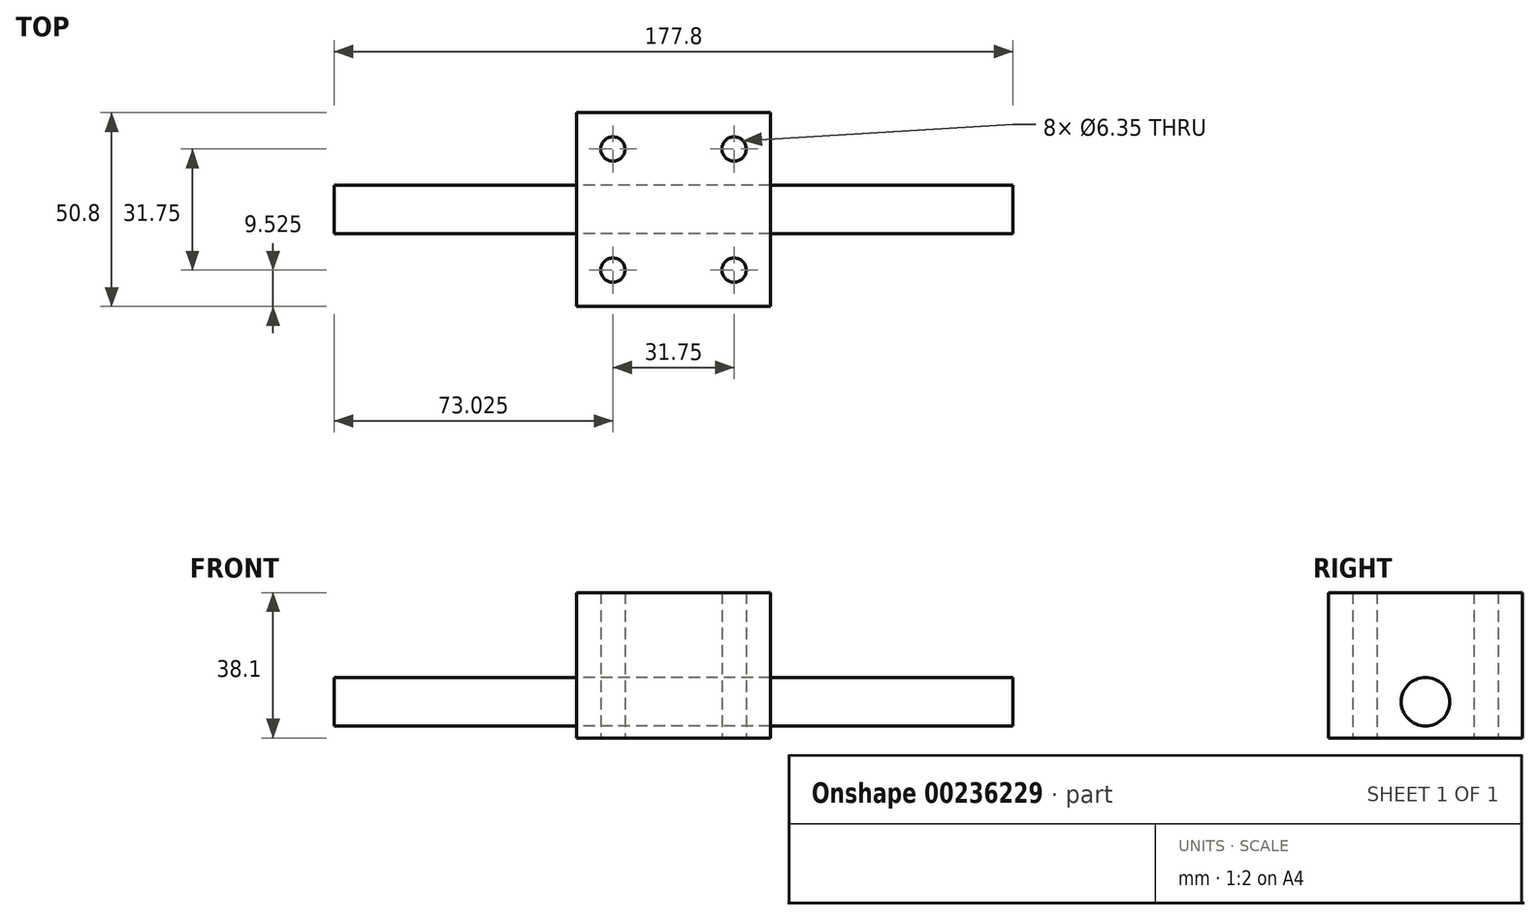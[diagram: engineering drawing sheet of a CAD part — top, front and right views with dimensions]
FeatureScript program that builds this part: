
annotation { "Feature Type Name" : "Feature", "Feature Type Description" : "" }
export const myFeature = defineFeature(function(context is Context, id is Id, definition is map)
    precondition{}
    {
        {
            var Q0;
            Q0=qCreatedBy(makeId("Top.planeOp"),FACE);
            var sketch = newSketch(context, id + "F0", { "sketchPlane" : qUnion([Q0])});
            skLineSegment(sketch, "E0.bottom", {"start": v(25.4, -25.4) * mm, "end": v(-25.4, -25.4) * mm});
            skLineSegment(sketch, "E0.top", {"start": v(25.4, 25.4) * mm, "end": v(-25.4, 25.4) * mm});
            skLineSegment(sketch, "E0.left", {"start": v(25.4, -25.4) * mm, "end": v(25.4, 25.4) * mm});
            skLineSegment(sketch, "E0.right", {"start": v(-25.4, -25.4) * mm, "end": v(-25.4, 25.4) * mm});
            skPoint(sketch, "E0.middle", {"position": v(0, 0) * mm});
            skCircle(sketch, "E1", {"center": v(-15.88, 15.87) * mm, "radius": 3.18 * mm});
            skCircle(sketch, "E2.MirrorC", {"center": v(15.88, 15.87) * mm, "radius": 3.18 * mm});
            skCircle(sketch, "E3.MirrorC", {"center": v(15.88, -15.87) * mm, "radius": 3.18 * mm});
            skCircle(sketch, "E4.MirrorC", {"center": v(-15.88, -15.87) * mm, "radius": 3.18 * mm});
            skSolve(sketch);
        }
        {
            var Q0;
            Q0 = qSketchRegion(id + "F0", true);
            extrude(context, id + "F1", {"entities" : qUnion([Q0]), "endBound" : BoundingType.SYMMETRIC, "depth" : 38.1 * mm});
        }
        {
            var Q0;
            Q0=makeQuery(id+"F1.opExtrude","SWEPT_BODY",BODY,{"disambiguationData":[OSD([sQuery(id+"F0.wireOp",EDGE,"E0.bottom"),sQuery(id+"F0.wireOp",EDGE,"E0.top"),sQuery(id+"F0.wireOp",EDGE,"E0.left"),sQuery(id+"F0.wireOp",EDGE,"E0.right"),sQuery(id+"F0.wireOp",EDGE,"E1"),sQuery(id+"F0.wireOp",EDGE,"E2.MirrorC"),sQuery(id+"F0.wireOp",EDGE,"E3.MirrorC"),sQuery(id+"F0.wireOp",EDGE,"E4.MirrorC")])]});
            var Q1;
            Q1=qCreatedBy(makeId("Right.planeOp"),FACE);
            mirror(context, id + "F2", {"entities" : qUnion([Q0]), "mirrorPlane" : qUnion([Q1])});
        }
        {
            var Q0;
            Q0=qCreatedBy(makeId("Right.planeOp"),FACE);
            var sketch = newSketch(context, id + "F3", { "sketchPlane" : qUnion([Q0])});
            skCircle(sketch, "E5", {"center": v(0, -9.53) * mm, "radius": 6.35 * mm});
            skSolve(sketch);
        }
        {
            var Q0;
            Q0 = qSketchRegion(id + "F3", true);
            extrude(context, id + "F4", {"entities" : qUnion([Q0]), "endBound" : BoundingType.SYMMETRIC, "depth" : 177.8 * mm});
        }
    });
